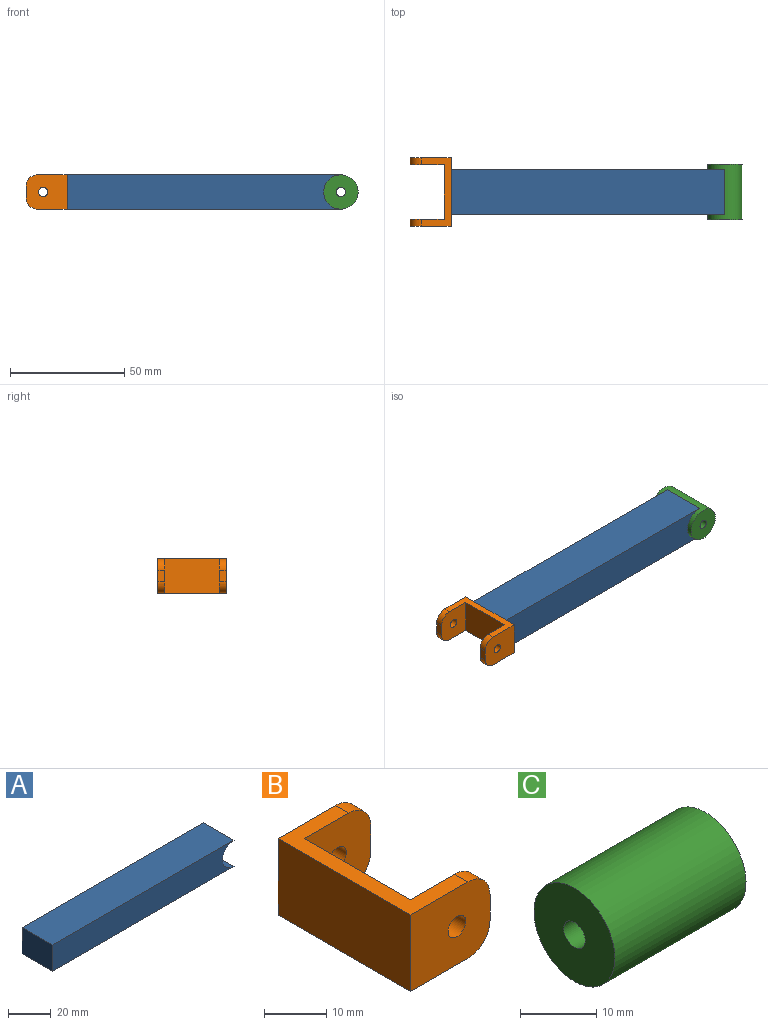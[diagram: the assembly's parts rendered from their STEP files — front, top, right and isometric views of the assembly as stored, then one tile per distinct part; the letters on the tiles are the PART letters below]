
ASSEMBLY  parts=3 mates=5
PART A: 6 faces, bbox 120x20x15 mm
  f0: plane 120x20mm, normal (0,0,1), area 2400mm2, adj f1,f3,f4,f5
  f1: plane 120x15mm, normal (0,-1,0), area 1711.6mm2, adj f0,f2,f4,f5
  f2: plane 120x20mm, normal (0,0,-1), area 2400mm2, adj f1,f3,f4,f5
  f3: plane 120x15mm, normal (0,1,0), area 1711.6mm2, adj f0,f2,f4,f5
  f4: plane 20x15mm, normal (-1,0,0), area 300mm2, adj f0,f1,f2,f3
  f5: cylinder r=7.5mm len=20mm, axis (0,1,0), area 471.2mm2, adj f0,f1,f2,f3
PART B: 16 faces, bbox 18x30x15 mm
  f0: plane 5x3mm, normal (1,0,0), area 15mm2, adj f4,f8,f12,f13
  f1: plane 30x13mm, normal (0,0,1), area 150mm2, adj f2,f4,f6,f7,f8,f9,f12,f15
  f2: plane 18x15mm, normal (0,-1,0), area 246.7mm2, adj f1,f3,f5,f6,f11,f14,f15
  f3: plane 30x13mm, normal (0,0,-1), area 150mm2, adj f2,f4,f6,f7,f8,f9,f13,f14
  f4: plane 18x15mm, normal (0,1,0), area 246.7mm2, adj f0,f1,f3,f6,f10,f12,f13
  f5: plane 5x3mm, normal (1,0,0), area 15mm2, adj f2,f7,f14,f15
  f6: plane 30x15mm, normal (-1,0,0), area 450mm2, adj f1,f2,f3,f4
  f7: plane 15x15mm, normal (0,1,0), area 201.7mm2, adj f1,f3,f5,f9,f11,f14,f15
  f8: plane 15x15mm, normal (0,-1,0), area 201.7mm2, adj f0,f1,f3,f9,f10,f12,f13
  f9: plane 24x15mm, normal (1,0,0), area 360mm2, adj f1,f3,f7,f8
  f10: cylinder r=2mm len=4mm, axis (0,-1,0), area 37.7mm2, adj f4,f8
  f11: cylinder r=2mm len=4mm, axis (0,-1,0), area 37.7mm2, adj f2,f7
  f12: cylinder r=5mm len=5mm, axis (0,1,0), area 23.6mm2, adj f0,f1,f4,f8
  f13: cylinder r=5mm len=5mm, axis (0,-1,0), area 23.6mm2, adj f0,f3,f4,f8
  f14: cylinder r=5mm len=5mm, axis (0,-1,0), area 23.6mm2, adj f2,f3,f5,f7
  f15: cylinder r=5mm len=5mm, axis (0,1,0), area 23.6mm2, adj f1,f2,f5,f7
PART C: 4 faces, bbox 24.3x15x15 mm
  f0: cylinder r=2mm len=24.3mm, axis (-1,0,0), area 305.4mm2, adj f2,f3
  f1: cylinder r=7.5mm len=24.3mm, axis (-1,0,0), area 1145.1mm2, adj f2,f3
  f2: plane 15x15mm, normal (1,0,0), area 164.1mm2, adj f0,f1
  f3: plane 15x15mm, normal (-1,0,0), area 164.1mm2, adj f0,f1
PLACE A t=(-17.37,16.61,-22.95)mm fixed
PLACE B rot(axis=(0,1,0),180deg) t=(-17.37,111.19,18.6)mm
PLACE C rot(axis=(0.58,0.58,0.58),120deg) t=(62.12,-9.09,31.32)mm
MATE planar C.f0 <-> A.f5  axis (0,-1,0) through (102.63,-9.09,-21.44)mm
MATE planar B.f6 <-> A.f4  axis (1,0,0) through (-17.37,3.06,-21.44)mm
MATE planar A.f3 <-> B.f10  axis (0,1,0) through (39.7,13.06,-21.44)mm
MATE planar A.f2 <-> B.f1  axis (0,0,-1) through (42.63,3.06,-28.94)mm
MATE planar B.f6 <-> A.f4  axis (1,0,0) through (-17.37,3.06,-21.44)mm
